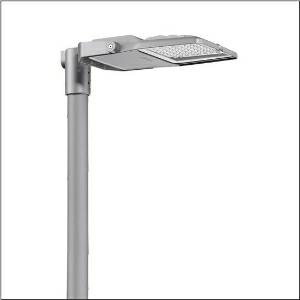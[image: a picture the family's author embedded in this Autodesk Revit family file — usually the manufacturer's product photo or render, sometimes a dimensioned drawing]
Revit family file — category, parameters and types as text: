
# Revit family: floodlight_fl_21_mini___pl43_5xa7776b4a3a_9af8
name_source: partatom
category: Lighting Fixtures
units: mm (PartAtom-declared; Revit-internal decimal feet)

## family parameters
Cut with Voids When Loaded = No
Host = Face
Light Source = No
Part Type = Normal
Room Calculation Point = No
Round Connector Dimension = Use Diameter
Shared = No

## types (1)
- --- (1 x LED, 6650 lm, 45.7 W, 4000K)
    Apparent Load = 46 VA
    CIE Flux Codes = 27 78 99 100 100
    Color Rendering = 70
    Color Temperature = 4000K
    Default Elevation = 1800 mm
    Description = Floodlight FL 21 mini, floodlight, primary light control with lens, of PMMA, primary optical cover: protective disc, of toughened safety glass, transparent, light distribution: PL43, light emission: direct distribution, installation type: surface-mounted, LED, High Power LED, rated luminous flux: 6.650lm, luminous efficacy: 146lm/W, light colour: 740, colour temperature: 4000K, control gear: D4iSmart Interface (Zhaga), control: overheat protection, constant luminous flux control, time-dependent luminous flux control, flexible luminous flux parameterisation, pre-setting: logarithmic dimming characteristic, with terminal, 6-pole, mains connection: 220..240V, AC, 50/60Hz, start of lifetime: 46W, end of service life: 48W, reduction: 22W, mast bracket, of diecast aluminium, powder-coated, Siteco® metallic grey (DB 702S), corrosivity category C5 mid according to DIN EN ISO 12944, suitable for swimming pools, chlorine-resistant, sealing non-destructively replaceable, mast bracket, of steel, galvanised, powder-coated, Siteco® metallic grey (DB 702S), Smart Interface below and above, protection rating (complete): IP66, insulation class (complete): insulation class II (safety insulation), certification: CE, ENEC, VDE, protection symbol: D, impact resistance: IK08, permissible operating ambient temperature: -40..+40°C, permissible operating ambient temperature for outdoor applications: -40..+50°C, standard: DIN EN 12944, LABS conformity tested according to VDMA 24364:2018-05, packaging unit: 1 piece

Light Distribution: PL43
    Height = 70 mm
    Lamp = 1 x LED
    Lamp Light Flux = 6650 lm
    Lamp Power = 45.7 W
    Lamp count = 1
    Length = 485 mm
    Luminous efficacy = 146 lm/W
    Manufacturer = Siteco
    ModVariant = No
    Model = 5XA7776B4A3A
    Number of Poles = 1
    OnlyDefault = Yes
    Power Factor = 1
    Product Name = Floodlight FL 21 mini | PL43
    Product group = floodlight | pylon annexe
    ProductGroupID = 6201
    Protection Class = Protection class II
    Protection Degree = IP 66
    RLX_Detail_Level = 1
    RLX_Emergency_Light_Flux = 0 lm
    RLX_Emergency_Type = 0
    RLX_Emergency_Type_DB = No
    RlxData = <blob elided: 100921 chars, md5=d6552ac1>
    Socket = socket
    Standby Power = 0 W
    System Light Flux = 6650 lm
    System Power = 46 W
    Type Comments = factory setting: luminous flux: 100 % | dim-lin: 254 | 463 mA
    Type Image = l_1007125.jpg
    URL = http://relux.com
    VarID = @adj_116863
    Voltage = 0 V
    Weight = 0.00 kg
    Width = 337 mm

## geometry (parser evidence)
native form markers: Blend x4, Sweep x12
no freeform markers — native parametric forms only
